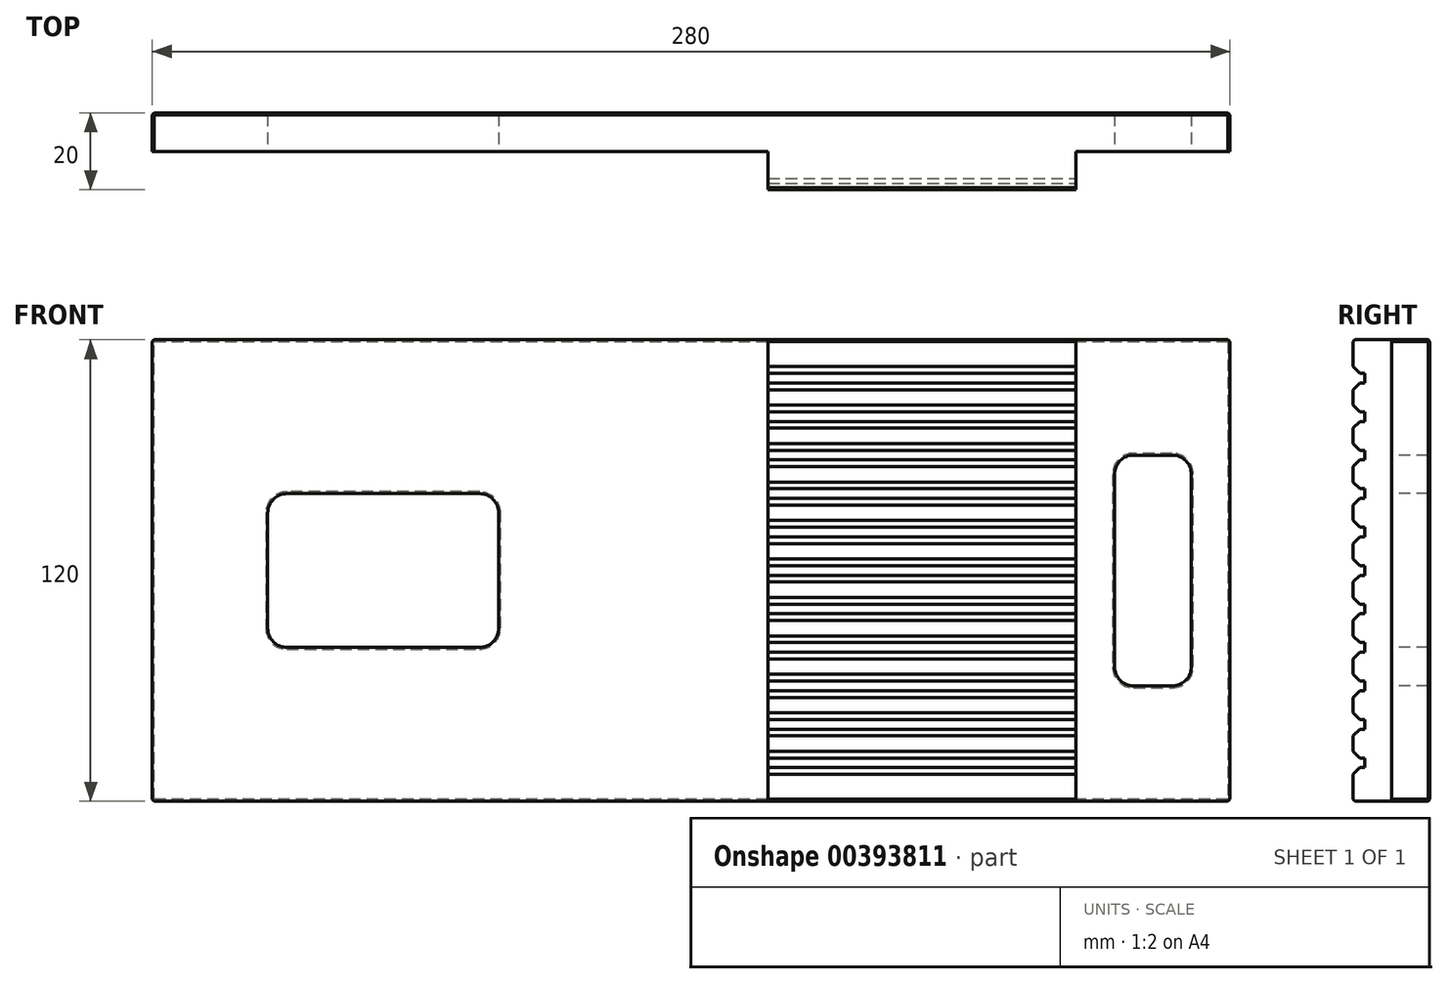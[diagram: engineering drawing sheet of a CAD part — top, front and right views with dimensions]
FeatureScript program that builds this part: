
annotation { "Feature Type Name" : "Feature", "Feature Type Description" : "" }
export const myFeature = defineFeature(function(context is Context, id is Id, definition is map)
    precondition{}
    {
        {
            var Q0;
            Q0=qCreatedBy(makeId("Front.planeOp"),FACE);
            var sketch = newSketch(context, id + "F0", { "sketchPlane" : qUnion([Q0])});
            skLineSegment(sketch, "E0.bottom", {"start": v(140, -60) * mm, "end": v(-140, -60) * mm});
            skLineSegment(sketch, "E0.top", {"start": v(140, 60) * mm, "end": v(-140, 60) * mm});
            skLineSegment(sketch, "E0.left", {"start": v(140, -60) * mm, "end": v(140, 60) * mm});
            skLineSegment(sketch, "E0.right", {"start": v(-140, -60) * mm, "end": v(-140, 60) * mm});
            skPoint(sketch, "E0.middle", {"position": v(0, 0) * mm});
            skSolve(sketch);
        }
        {
            var Q0;
            Q0 = qSketchRegion(id + "F0", true);
            extrude(context, id + "F1", {"entities" : qUnion([Q0]), "depth" : 20 * mm});
        }
        {
            var Q0;
            Q0=makeQuery(id+"F1.opExtrude","CAP_FACE",FACE,{"disambiguationData":[OSD([sQuery(id+"F0.wireOp",EDGE,"E0.bottom"),sQuery(id+"F0.wireOp",EDGE,"E0.top"),sQuery(id+"F0.wireOp",EDGE,"E0.left"),sQuery(id+"F0.wireOp",EDGE,"E0.right")])],"isStart":false});
            var sketch = newSketch(context, id + "F2", { "sketchPlane" : qUnion([Q0])});
            skLineSegment(sketch, "E1.bottom", {"start": v(-140, 60) * mm, "end": v(20, 60) * mm});
            skLineSegment(sketch, "E1.top", {"start": v(-140, -60) * mm, "end": v(20, -60) * mm});
            skLineSegment(sketch, "E1.left", {"start": v(-140, 60) * mm, "end": v(-140, -60) * mm});
            skLineSegment(sketch, "E1.right", {"start": v(20, 60) * mm, "end": v(20, -60) * mm});
            skSolve(sketch);
        }
        {
            var Q0;
            Q0 = qSketchRegion(id + "F2", true);
            extrude(context, id + "F3", {"entities" : qUnion([Q0]), "operationType" : NewBodyOperationType.REMOVE, "oppositeDirection" : true, "depth" : 10 * mm});
        }
        {
            var Q0;
            Q0=makeQuery(id+"F3.boolean.opBoolean","COPY",FACE,{"derivedFrom":makeQuery(id+"F3.opExtrude","CAP_FACE",FACE,{"disambiguationData":[OSD([sQuery(id+"F2.wireOp",EDGE,"E1.bottom"),sQuery(id+"F2.wireOp",EDGE,"E1.top"),sQuery(id+"F2.wireOp",EDGE,"E1.left"),sQuery(id+"F2.wireOp",EDGE,"E1.right")])],"isStart":false})});
            var sketch = newSketch(context, id + "F4", { "sketchPlane" : qUnion([Q0])});
            skLineSegment(sketch, "E2.bottom", {"start": v(-55, -20) * mm, "end": v(-105, -20) * mm});
            skLineSegment(sketch, "E2.top", {"start": v(-55, 20) * mm, "end": v(-105, 20) * mm});
            skLineSegment(sketch, "E2.left", {"start": v(-50, -15) * mm, "end": v(-50, 15) * mm});
            skLineSegment(sketch, "E2.right", {"start": v(-110, -15) * mm, "end": v(-110, 15) * mm});
            skPoint(sketch, "E2.middle", {"position": v(-80, 0) * mm});
            skPoint(sketch, "E3.visualSharp", {"position": v(-50, 20) * mm});
            skArc(sketch, "E3.filletArc", {"start": v(-50, 15) * mm, "mid": v(-51.46, 18.54) * mm, "end": v(-55, 20) * mm});
            skPoint(sketch, "E4.visualSharp", {"position": v(-50, -20) * mm});
            skArc(sketch, "E4.filletArc", {"start": v(-55, -20) * mm, "mid": v(-51.46, -18.54) * mm, "end": v(-50, -15) * mm});
            skPoint(sketch, "E5.visualSharp", {"position": v(-110, -20) * mm});
            skArc(sketch, "E5.filletArc", {"start": v(-110, -15) * mm, "mid": v(-108.54, -18.54) * mm, "end": v(-105, -20) * mm});
            skPoint(sketch, "E6.visualSharp", {"position": v(-110, 20) * mm});
            skArc(sketch, "E6.filletArc", {"start": v(-105, 20) * mm, "mid": v(-108.54, 18.54) * mm, "end": v(-110, 15) * mm});
            skSolve(sketch);
        }
        {
            var Q0;
            Q0 = qSketchRegion(id + "F4", true);
            extrude(context, id + "F5", {"entities" : qUnion([Q0]), "operationType" : NewBodyOperationType.REMOVE, "oppositeDirection" : true, "depth" : 25 * mm});
        }
        {
            var Q0;
            Q0=makeQuery(id+"F1.opExtrude","CAP_FACE",FACE,{"disambiguationData":[OSD([sQuery(id+"F0.wireOp",EDGE,"E0.bottom"),sQuery(id+"F0.wireOp",EDGE,"E0.top"),sQuery(id+"F0.wireOp",EDGE,"E0.left"),sQuery(id+"F0.wireOp",EDGE,"E0.right")])],"isStart":false});
            var sketch = newSketch(context, id + "F6", { "sketchPlane" : qUnion([Q0])});
            skLineSegment(sketch, "E7.bottom", {"start": v(140, -60) * mm, "end": v(100, -60) * mm});
            skLineSegment(sketch, "E7.top", {"start": v(140, 60) * mm, "end": v(100, 60) * mm});
            skLineSegment(sketch, "E7.left", {"start": v(140, -60) * mm, "end": v(140, 60) * mm});
            skLineSegment(sketch, "E7.right", {"start": v(100, -60) * mm, "end": v(100, 60) * mm});
            skPoint(sketch, "E7.middle", {"position": v(120, 0) * mm});
            skSolve(sketch);
        }
        {
            var Q0;
            Q0 = qSketchRegion(id + "F6", true);
            extrude(context, id + "F7", {"entities" : qUnion([Q0]), "operationType" : NewBodyOperationType.REMOVE, "oppositeDirection" : true, "depth" : 10 * mm});
        }
        {
            var Q0;
            Q0=makeQuery(id+"F7.boolean.opBoolean","COPY",FACE,{"derivedFrom":makeQuery(id+"F7.opExtrude","CAP_FACE",FACE,{"disambiguationData":[OSD([sQuery(id+"F6.wireOp",EDGE,"E7.bottom"),sQuery(id+"F6.wireOp",EDGE,"E7.top"),sQuery(id+"F6.wireOp",EDGE,"E7.left"),sQuery(id+"F6.wireOp",EDGE,"E7.right")])],"isStart":false})});
            var sketch = newSketch(context, id + "F8", { "sketchPlane" : qUnion([Q0])});
            skLineSegment(sketch, "E8.bottom", {"start": v(115, -30) * mm, "end": v(125, -30) * mm});
            skLineSegment(sketch, "E8.top", {"start": v(115, 30) * mm, "end": v(125, 30) * mm});
            skLineSegment(sketch, "E8.left", {"start": v(110, -25) * mm, "end": v(110, 25) * mm});
            skLineSegment(sketch, "E8.right", {"start": v(130, -25) * mm, "end": v(130, 25) * mm});
            skPoint(sketch, "E8.middle", {"position": v(120, 0) * mm});
            skPoint(sketch, "E9", {"position": v(140, 0) * mm});
            skPoint(sketch, "E10.visualSharp", {"position": v(110, 30) * mm});
            skArc(sketch, "E10.filletArc", {"start": v(115, 30) * mm, "mid": v(111.46, 28.54) * mm, "end": v(110, 25) * mm});
            skPoint(sketch, "E11.visualSharp", {"position": v(130, 30) * mm});
            skArc(sketch, "E11.filletArc", {"start": v(130, 25) * mm, "mid": v(128.54, 28.54) * mm, "end": v(125, 30) * mm});
            skPoint(sketch, "E12.visualSharp", {"position": v(130, -30) * mm});
            skArc(sketch, "E12.filletArc", {"start": v(125, -30) * mm, "mid": v(128.54, -28.54) * mm, "end": v(130, -25) * mm});
            skPoint(sketch, "E13.visualSharp", {"position": v(110, -30) * mm});
            skArc(sketch, "E13.filletArc", {"start": v(110, -25) * mm, "mid": v(111.46, -28.54) * mm, "end": v(115, -30) * mm});
            skSolve(sketch);
        }
        {
            var Q0;
            Q0 = qSketchRegion(id + "F8", true);
            extrude(context, id + "F9", {"entities" : qUnion([Q0]), "operationType" : NewBodyOperationType.REMOVE, "endBound" : BoundingType.THROUGH_ALL, "oppositeDirection" : true, "depth" : 25 * mm});
        }
        {
            var Q0;
            Q0=makeQuery(id+"F7.boolean.opBoolean","COPY",FACE,{"derivedFrom":makeQuery(id+"F7.opExtrude","SWEPT_FACE",FACE,{"disambiguationData":[OSD([sQuery(id+"F6.wireOp",EDGE,"E7.right")])]})});
            var sketch = newSketch(context, id + "F10", { "sketchPlane" : qUnion([Q0])});
            skLineSegment(sketch, "E14", {"start": v(-20, -50) * mm, "end": v(-17, -50) * mm, "construction": true});
            skLineSegment(sketch, "E15", {"start": v(-17, -51.25) * mm, "end": v(-17, -48.75) * mm});
            skLineSegment(sketch, "E16", {"start": v(-17, -51.25) * mm, "end": v(-18.25, -51.25) * mm});
            skLineSegment(sketch, "E17", {"start": v(-17, -48.75) * mm, "end": v(-18.25, -48.75) * mm});
            skLineSegment(sketch, "E18", {"start": v(-20, -53) * mm, "end": v(-18.25, -51.25) * mm});
            skLineSegment(sketch, "E19", {"start": v(-18.25, -48.75) * mm, "end": v(-20, -47) * mm});
            skLineSegment(sketch, "E20", {"start": v(-20, -53) * mm, "end": v(-20, -47) * mm});
            skLineSegment(sketch, "E21.0.1.0", {"start": v(-20, -43) * mm, "end": v(-20, -37) * mm});
            skLineSegment(sketch, "E21.0.1.1", {"start": v(-20, -43) * mm, "end": v(-18.25, -41.25) * mm});
            skLineSegment(sketch, "E21.0.1.2", {"start": v(-17, -41.25) * mm, "end": v(-18.25, -41.25) * mm});
            skLineSegment(sketch, "E21.0.1.3", {"start": v(-17, -41.25) * mm, "end": v(-17, -38.75) * mm});
            skLineSegment(sketch, "E21.0.1.4", {"start": v(-17, -38.75) * mm, "end": v(-18.25, -38.75) * mm});
            skLineSegment(sketch, "E21.0.1.5", {"start": v(-18.25, -38.75) * mm, "end": v(-20, -37) * mm});
            skLineSegment(sketch, "E21.0.2.0", {"start": v(-20, -33) * mm, "end": v(-20, -27) * mm});
            skLineSegment(sketch, "E21.0.2.1", {"start": v(-20, -33) * mm, "end": v(-18.25, -31.25) * mm});
            skLineSegment(sketch, "E21.0.2.2", {"start": v(-17, -31.25) * mm, "end": v(-18.25, -31.25) * mm});
            skLineSegment(sketch, "E21.0.2.3", {"start": v(-17, -31.25) * mm, "end": v(-17, -28.75) * mm});
            skLineSegment(sketch, "E21.0.2.4", {"start": v(-17, -28.75) * mm, "end": v(-18.25, -28.75) * mm});
            skLineSegment(sketch, "E21.0.2.5", {"start": v(-18.25, -28.75) * mm, "end": v(-20, -27) * mm});
            skLineSegment(sketch, "E21.0.3.0", {"start": v(-20, -23) * mm, "end": v(-20, -17) * mm});
            skLineSegment(sketch, "E21.0.3.1", {"start": v(-20, -23) * mm, "end": v(-18.25, -21.25) * mm});
            skLineSegment(sketch, "E21.0.3.2", {"start": v(-17, -21.25) * mm, "end": v(-18.25, -21.25) * mm});
            skLineSegment(sketch, "E21.0.3.3", {"start": v(-17, -21.25) * mm, "end": v(-17, -18.75) * mm});
            skLineSegment(sketch, "E21.0.3.4", {"start": v(-17, -18.75) * mm, "end": v(-18.25, -18.75) * mm});
            skLineSegment(sketch, "E21.0.3.5", {"start": v(-18.25, -18.75) * mm, "end": v(-20, -17) * mm});
            skLineSegment(sketch, "E21.0.4.0", {"start": v(-20, -13) * mm, "end": v(-20, -7) * mm});
            skLineSegment(sketch, "E21.0.4.1", {"start": v(-20, -13) * mm, "end": v(-18.25, -11.25) * mm});
            skLineSegment(sketch, "E21.0.4.2", {"start": v(-17, -11.25) * mm, "end": v(-18.25, -11.25) * mm});
            skLineSegment(sketch, "E21.0.4.3", {"start": v(-17, -11.25) * mm, "end": v(-17, -8.75) * mm});
            skLineSegment(sketch, "E21.0.4.4", {"start": v(-17, -8.75) * mm, "end": v(-18.25, -8.75) * mm});
            skLineSegment(sketch, "E21.0.4.5", {"start": v(-18.25, -8.75) * mm, "end": v(-20, -7) * mm});
            skLineSegment(sketch, "E21.0.5.0", {"start": v(-20, -3) * mm, "end": v(-20, 3) * mm});
            skLineSegment(sketch, "E21.0.5.1", {"start": v(-20, -3) * mm, "end": v(-18.25, -1.25) * mm});
            skLineSegment(sketch, "E21.0.5.2", {"start": v(-17, -1.25) * mm, "end": v(-18.25, -1.25) * mm});
            skLineSegment(sketch, "E21.0.5.3", {"start": v(-17, -1.25) * mm, "end": v(-17, 1.25) * mm});
            skLineSegment(sketch, "E21.0.5.4", {"start": v(-17, 1.25) * mm, "end": v(-18.25, 1.25) * mm});
            skLineSegment(sketch, "E21.0.5.5", {"start": v(-18.25, 1.25) * mm, "end": v(-20, 3) * mm});
            skLineSegment(sketch, "E21.0.6.0", {"start": v(-20, 7) * mm, "end": v(-20, 13) * mm});
            skLineSegment(sketch, "E21.0.6.1", {"start": v(-20, 7) * mm, "end": v(-18.25, 8.75) * mm});
            skLineSegment(sketch, "E21.0.6.2", {"start": v(-17, 8.75) * mm, "end": v(-18.25, 8.75) * mm});
            skLineSegment(sketch, "E21.0.6.3", {"start": v(-17, 8.75) * mm, "end": v(-17, 11.25) * mm});
            skLineSegment(sketch, "E21.0.6.4", {"start": v(-17, 11.25) * mm, "end": v(-18.25, 11.25) * mm});
            skLineSegment(sketch, "E21.0.6.5", {"start": v(-18.25, 11.25) * mm, "end": v(-20, 13) * mm});
            skLineSegment(sketch, "E21.0.7.0", {"start": v(-20, 17) * mm, "end": v(-20, 23) * mm});
            skLineSegment(sketch, "E21.0.7.1", {"start": v(-20, 17) * mm, "end": v(-18.25, 18.75) * mm});
            skLineSegment(sketch, "E21.0.7.2", {"start": v(-17, 18.75) * mm, "end": v(-18.25, 18.75) * mm});
            skLineSegment(sketch, "E21.0.7.3", {"start": v(-17, 18.75) * mm, "end": v(-17, 21.25) * mm});
            skLineSegment(sketch, "E21.0.7.4", {"start": v(-17, 21.25) * mm, "end": v(-18.25, 21.25) * mm});
            skLineSegment(sketch, "E21.0.7.5", {"start": v(-18.25, 21.25) * mm, "end": v(-20, 23) * mm});
            skLineSegment(sketch, "E21.0.8.0", {"start": v(-20, 27) * mm, "end": v(-20, 33) * mm});
            skLineSegment(sketch, "E21.0.8.1", {"start": v(-20, 27) * mm, "end": v(-18.25, 28.75) * mm});
            skLineSegment(sketch, "E21.0.8.2", {"start": v(-17, 28.75) * mm, "end": v(-18.25, 28.75) * mm});
            skLineSegment(sketch, "E21.0.8.3", {"start": v(-17, 28.75) * mm, "end": v(-17, 31.25) * mm});
            skLineSegment(sketch, "E21.0.8.4", {"start": v(-17, 31.25) * mm, "end": v(-18.25, 31.25) * mm});
            skLineSegment(sketch, "E21.0.8.5", {"start": v(-18.25, 31.25) * mm, "end": v(-20, 33) * mm});
            skLineSegment(sketch, "E21.0.9.0", {"start": v(-20, 37) * mm, "end": v(-20, 43) * mm});
            skLineSegment(sketch, "E21.0.9.1", {"start": v(-20, 37) * mm, "end": v(-18.25, 38.75) * mm});
            skLineSegment(sketch, "E21.0.9.2", {"start": v(-17, 38.75) * mm, "end": v(-18.25, 38.75) * mm});
            skLineSegment(sketch, "E21.0.9.3", {"start": v(-17, 38.75) * mm, "end": v(-17, 41.25) * mm});
            skLineSegment(sketch, "E21.0.9.4", {"start": v(-17, 41.25) * mm, "end": v(-18.25, 41.25) * mm});
            skLineSegment(sketch, "E21.0.9.5", {"start": v(-18.25, 41.25) * mm, "end": v(-20, 43) * mm});
            skLineSegment(sketch, "E21.0.10.0", {"start": v(-20, 47) * mm, "end": v(-20, 53) * mm});
            skLineSegment(sketch, "E21.0.10.1", {"start": v(-20, 47) * mm, "end": v(-18.25, 48.75) * mm});
            skLineSegment(sketch, "E21.0.10.2", {"start": v(-17, 48.75) * mm, "end": v(-18.25, 48.75) * mm});
            skLineSegment(sketch, "E21.0.10.3", {"start": v(-17, 48.75) * mm, "end": v(-17, 51.25) * mm});
            skLineSegment(sketch, "E21.0.10.4", {"start": v(-17, 51.25) * mm, "end": v(-18.25, 51.25) * mm});
            skLineSegment(sketch, "E21.0.10.5", {"start": v(-18.25, 51.25) * mm, "end": v(-20, 53) * mm});
            skLineSegment(sketch, "E21.direction1", {"start": v(-20, -53) * mm, "end": v(5, -53) * mm, "construction": true});
            skLineSegment(sketch, "E21.direction2", {"start": v(-20, -53) * mm, "end": v(-20, -43) * mm, "construction": true});
            skSolve(sketch);
        }
        {
            var Q0;
            Q0 = qSketchRegion(id + "F10", true);
            extrude(context, id + "F11", {"entities" : qUnion([Q0]), "operationType" : NewBodyOperationType.REMOVE, "endBound" : BoundingType.THROUGH_ALL, "oppositeDirection" : true, "depth" : 25 * mm});
        }
        {
            var Q0;
            Q0=makeQuery(id+"F1.opExtrude","CAP_EDGE",EDGE,{"disambiguationData":[OSD([sQuery(id+"F0.wireOp",EDGE,"E0.bottom")])],"isStart":false});
            var Q1;
            {var subQ0=sQuery(id+"F0.wireOp",EDGE,"E0.bottom");var subQ1=sQuery(id+"F6.wireOp",EDGE,"E7.right");Q1=makeQuery(id+"F11.boolean.opBoolean","SPLIT",EDGE,{"disambiguationData":[TD([makeQuery(id+"F1.opExtrude","SWEPT_FACE",FACE,{"disambiguationData":[OSD([subQ0])]})])],"derivedFrom":makeQuery(id+"F7.boolean.opBoolean","COPY",EDGE,{"derivedFrom":makeQuery(id+"F7.opExtrude","CAP_EDGE",EDGE,{"disambiguationData":[OSD([subQ1])],"isStart":true})})});}
            var Q2;
            {var subQ0=sQuery(id+"F6.wireOp",EDGE,"E7.right");Q2=makeQuery(id+"F11.boolean.opBoolean","SPLIT",EDGE,{"disambiguationData":[TD([makeQuery(id+"F11.opExtrude","SWEPT_FACE",FACE,{"disambiguationData":[OSD([sQuery(id+"F10.wireOp",EDGE,"E19")])]})])],"derivedFrom":makeQuery(id+"F7.boolean.opBoolean","COPY",EDGE,{"derivedFrom":makeQuery(id+"F7.opExtrude","CAP_EDGE",EDGE,{"disambiguationData":[OSD([subQ0])],"isStart":true})})});}
            var Q3;
            {var subQ0=sQuery(id+"F6.wireOp",EDGE,"E7.right");Q3=makeQuery(id+"F11.boolean.opBoolean","SPLIT",EDGE,{"disambiguationData":[TD([makeQuery(id+"F11.opExtrude","SWEPT_FACE",FACE,{"disambiguationData":[OSD([sQuery(id+"F10.wireOp",EDGE,"E21.0.2.5")])]})])],"derivedFrom":makeQuery(id+"F7.boolean.opBoolean","COPY",EDGE,{"derivedFrom":makeQuery(id+"F7.opExtrude","CAP_EDGE",EDGE,{"disambiguationData":[OSD([subQ0])],"isStart":true})})});}
            var Q4;
            {var subQ0=sQuery(id+"F6.wireOp",EDGE,"E7.right");Q4=makeQuery(id+"F11.boolean.opBoolean","SPLIT",EDGE,{"disambiguationData":[TD([makeQuery(id+"F11.opExtrude","SWEPT_FACE",FACE,{"disambiguationData":[OSD([sQuery(id+"F10.wireOp",EDGE,"E21.0.3.5")])]})])],"derivedFrom":makeQuery(id+"F7.boolean.opBoolean","COPY",EDGE,{"derivedFrom":makeQuery(id+"F7.opExtrude","CAP_EDGE",EDGE,{"disambiguationData":[OSD([subQ0])],"isStart":true})})});}
            var Q5;
            {var subQ0=sQuery(id+"F6.wireOp",EDGE,"E7.right");Q5=makeQuery(id+"F11.boolean.opBoolean","SPLIT",EDGE,{"disambiguationData":[TD([makeQuery(id+"F11.opExtrude","SWEPT_FACE",FACE,{"disambiguationData":[OSD([sQuery(id+"F10.wireOp",EDGE,"E21.0.1.5")])]})])],"derivedFrom":makeQuery(id+"F7.boolean.opBoolean","COPY",EDGE,{"derivedFrom":makeQuery(id+"F7.opExtrude","CAP_EDGE",EDGE,{"disambiguationData":[OSD([subQ0])],"isStart":true})})});}
            var Q6;
            {var subQ0=sQuery(id+"F6.wireOp",EDGE,"E7.right");Q6=makeQuery(id+"F11.boolean.opBoolean","SPLIT",EDGE,{"disambiguationData":[TD([makeQuery(id+"F11.opExtrude","SWEPT_FACE",FACE,{"disambiguationData":[OSD([sQuery(id+"F10.wireOp",EDGE,"E21.0.4.5")])]})])],"derivedFrom":makeQuery(id+"F7.boolean.opBoolean","COPY",EDGE,{"derivedFrom":makeQuery(id+"F7.opExtrude","CAP_EDGE",EDGE,{"disambiguationData":[OSD([subQ0])],"isStart":true})})});}
            var Q7;
            {var subQ0=sQuery(id+"F6.wireOp",EDGE,"E7.right");Q7=makeQuery(id+"F11.boolean.opBoolean","SPLIT",EDGE,{"disambiguationData":[TD([makeQuery(id+"F11.opExtrude","SWEPT_FACE",FACE,{"disambiguationData":[OSD([sQuery(id+"F10.wireOp",EDGE,"E21.0.5.5")])]})])],"derivedFrom":makeQuery(id+"F7.boolean.opBoolean","COPY",EDGE,{"derivedFrom":makeQuery(id+"F7.opExtrude","CAP_EDGE",EDGE,{"disambiguationData":[OSD([subQ0])],"isStart":true})})});}
            var Q8;
            {var subQ0=sQuery(id+"F6.wireOp",EDGE,"E7.right");Q8=makeQuery(id+"F11.boolean.opBoolean","SPLIT",EDGE,{"disambiguationData":[TD([makeQuery(id+"F11.opExtrude","SWEPT_FACE",FACE,{"disambiguationData":[OSD([sQuery(id+"F10.wireOp",EDGE,"E21.0.6.5")])]})])],"derivedFrom":makeQuery(id+"F7.boolean.opBoolean","COPY",EDGE,{"derivedFrom":makeQuery(id+"F7.opExtrude","CAP_EDGE",EDGE,{"disambiguationData":[OSD([subQ0])],"isStart":true})})});}
            var Q9;
            {var subQ0=sQuery(id+"F6.wireOp",EDGE,"E7.right");Q9=makeQuery(id+"F11.boolean.opBoolean","SPLIT",EDGE,{"disambiguationData":[TD([makeQuery(id+"F11.opExtrude","SWEPT_FACE",FACE,{"disambiguationData":[OSD([sQuery(id+"F10.wireOp",EDGE,"E21.0.7.5")])]})])],"derivedFrom":makeQuery(id+"F7.boolean.opBoolean","COPY",EDGE,{"derivedFrom":makeQuery(id+"F7.opExtrude","CAP_EDGE",EDGE,{"disambiguationData":[OSD([subQ0])],"isStart":true})})});}
            var Q10;
            {var subQ0=sQuery(id+"F6.wireOp",EDGE,"E7.right");Q10=makeQuery(id+"F11.boolean.opBoolean","SPLIT",EDGE,{"disambiguationData":[TD([makeQuery(id+"F11.opExtrude","SWEPT_FACE",FACE,{"disambiguationData":[OSD([sQuery(id+"F10.wireOp",EDGE,"E21.0.8.5")])]})])],"derivedFrom":makeQuery(id+"F7.boolean.opBoolean","COPY",EDGE,{"derivedFrom":makeQuery(id+"F7.opExtrude","CAP_EDGE",EDGE,{"disambiguationData":[OSD([subQ0])],"isStart":true})})});}
            var Q11;
            {var subQ0=sQuery(id+"F6.wireOp",EDGE,"E7.right");Q11=makeQuery(id+"F11.boolean.opBoolean","SPLIT",EDGE,{"disambiguationData":[TD([makeQuery(id+"F11.opExtrude","SWEPT_FACE",FACE,{"disambiguationData":[OSD([sQuery(id+"F10.wireOp",EDGE,"E21.0.9.5")])]})])],"derivedFrom":makeQuery(id+"F7.boolean.opBoolean","COPY",EDGE,{"derivedFrom":makeQuery(id+"F7.opExtrude","CAP_EDGE",EDGE,{"disambiguationData":[OSD([subQ0])],"isStart":true})})});}
            var Q12;
            {var subQ0=sQuery(id+"F0.wireOp",EDGE,"E0.top");var subQ1=sQuery(id+"F6.wireOp",EDGE,"E7.right");Q12=makeQuery(id+"F11.boolean.opBoolean","SPLIT",EDGE,{"disambiguationData":[TD([makeQuery(id+"F1.opExtrude","SWEPT_FACE",FACE,{"disambiguationData":[OSD([subQ0])]})])],"derivedFrom":makeQuery(id+"F7.boolean.opBoolean","COPY",EDGE,{"derivedFrom":makeQuery(id+"F7.opExtrude","CAP_EDGE",EDGE,{"disambiguationData":[OSD([subQ1])],"isStart":true})})});}
            var Q13;
            Q13=makeQuery(id+"F1.opExtrude","CAP_EDGE",EDGE,{"disambiguationData":[OSD([sQuery(id+"F0.wireOp",EDGE,"E0.top")])],"isStart":false});
            var Q14;
            {var subQ0=sQuery(id+"F0.wireOp",EDGE,"E0.bottom");var subQ1=sQuery(id+"F2.wireOp",EDGE,"E1.right");Q14=makeQuery(id+"F11.boolean.opBoolean","SPLIT",EDGE,{"disambiguationData":[TD([makeQuery(id+"F1.opExtrude","SWEPT_FACE",FACE,{"disambiguationData":[OSD([subQ0])]})])],"derivedFrom":makeQuery(id+"F3.boolean.opBoolean","COPY",EDGE,{"derivedFrom":makeQuery(id+"F3.opExtrude","CAP_EDGE",EDGE,{"disambiguationData":[OSD([subQ1])],"isStart":true})})});}
            var Q15;
            {var subQ0=sQuery(id+"F2.wireOp",EDGE,"E1.right");Q15=makeQuery(id+"F11.boolean.opBoolean","SPLIT",EDGE,{"disambiguationData":[TD([makeQuery(id+"F11.opExtrude","SWEPT_FACE",FACE,{"disambiguationData":[OSD([sQuery(id+"F10.wireOp",EDGE,"E19")])]})])],"derivedFrom":makeQuery(id+"F3.boolean.opBoolean","COPY",EDGE,{"derivedFrom":makeQuery(id+"F3.opExtrude","CAP_EDGE",EDGE,{"disambiguationData":[OSD([subQ0])],"isStart":true})})});}
            var Q16;
            {var subQ0=sQuery(id+"F2.wireOp",EDGE,"E1.right");Q16=makeQuery(id+"F11.boolean.opBoolean","SPLIT",EDGE,{"disambiguationData":[TD([makeQuery(id+"F11.opExtrude","SWEPT_FACE",FACE,{"disambiguationData":[OSD([sQuery(id+"F10.wireOp",EDGE,"E21.0.1.5")])]})])],"derivedFrom":makeQuery(id+"F3.boolean.opBoolean","COPY",EDGE,{"derivedFrom":makeQuery(id+"F3.opExtrude","CAP_EDGE",EDGE,{"disambiguationData":[OSD([subQ0])],"isStart":true})})});}
            var Q17;
            {var subQ0=sQuery(id+"F2.wireOp",EDGE,"E1.right");Q17=makeQuery(id+"F11.boolean.opBoolean","SPLIT",EDGE,{"disambiguationData":[TD([makeQuery(id+"F11.opExtrude","SWEPT_FACE",FACE,{"disambiguationData":[OSD([sQuery(id+"F10.wireOp",EDGE,"E21.0.2.5")])]})])],"derivedFrom":makeQuery(id+"F3.boolean.opBoolean","COPY",EDGE,{"derivedFrom":makeQuery(id+"F3.opExtrude","CAP_EDGE",EDGE,{"disambiguationData":[OSD([subQ0])],"isStart":true})})});}
            var Q18;
            {var subQ0=sQuery(id+"F2.wireOp",EDGE,"E1.right");Q18=makeQuery(id+"F11.boolean.opBoolean","SPLIT",EDGE,{"disambiguationData":[TD([makeQuery(id+"F11.opExtrude","SWEPT_FACE",FACE,{"disambiguationData":[OSD([sQuery(id+"F10.wireOp",EDGE,"E21.0.3.5")])]})])],"derivedFrom":makeQuery(id+"F3.boolean.opBoolean","COPY",EDGE,{"derivedFrom":makeQuery(id+"F3.opExtrude","CAP_EDGE",EDGE,{"disambiguationData":[OSD([subQ0])],"isStart":true})})});}
            var Q19;
            {var subQ0=sQuery(id+"F2.wireOp",EDGE,"E1.right");Q19=makeQuery(id+"F11.boolean.opBoolean","SPLIT",EDGE,{"disambiguationData":[TD([makeQuery(id+"F11.opExtrude","SWEPT_FACE",FACE,{"disambiguationData":[OSD([sQuery(id+"F10.wireOp",EDGE,"E21.0.4.5")])]})])],"derivedFrom":makeQuery(id+"F3.boolean.opBoolean","COPY",EDGE,{"derivedFrom":makeQuery(id+"F3.opExtrude","CAP_EDGE",EDGE,{"disambiguationData":[OSD([subQ0])],"isStart":true})})});}
            var Q20;
            {var subQ0=sQuery(id+"F2.wireOp",EDGE,"E1.right");Q20=makeQuery(id+"F11.boolean.opBoolean","SPLIT",EDGE,{"disambiguationData":[TD([makeQuery(id+"F11.opExtrude","SWEPT_FACE",FACE,{"disambiguationData":[OSD([sQuery(id+"F10.wireOp",EDGE,"E21.0.5.5")])]})])],"derivedFrom":makeQuery(id+"F3.boolean.opBoolean","COPY",EDGE,{"derivedFrom":makeQuery(id+"F3.opExtrude","CAP_EDGE",EDGE,{"disambiguationData":[OSD([subQ0])],"isStart":true})})});}
            var Q21;
            {var subQ0=sQuery(id+"F2.wireOp",EDGE,"E1.right");Q21=makeQuery(id+"F11.boolean.opBoolean","SPLIT",EDGE,{"disambiguationData":[TD([makeQuery(id+"F11.opExtrude","SWEPT_FACE",FACE,{"disambiguationData":[OSD([sQuery(id+"F10.wireOp",EDGE,"E21.0.6.5")])]})])],"derivedFrom":makeQuery(id+"F3.boolean.opBoolean","COPY",EDGE,{"derivedFrom":makeQuery(id+"F3.opExtrude","CAP_EDGE",EDGE,{"disambiguationData":[OSD([subQ0])],"isStart":true})})});}
            var Q22;
            {var subQ0=sQuery(id+"F2.wireOp",EDGE,"E1.right");Q22=makeQuery(id+"F11.boolean.opBoolean","SPLIT",EDGE,{"disambiguationData":[TD([makeQuery(id+"F11.opExtrude","SWEPT_FACE",FACE,{"disambiguationData":[OSD([sQuery(id+"F10.wireOp",EDGE,"E21.0.7.5")])]})])],"derivedFrom":makeQuery(id+"F3.boolean.opBoolean","COPY",EDGE,{"derivedFrom":makeQuery(id+"F3.opExtrude","CAP_EDGE",EDGE,{"disambiguationData":[OSD([subQ0])],"isStart":true})})});}
            var Q23;
            {var subQ0=sQuery(id+"F0.wireOp",EDGE,"E0.top");var subQ1=sQuery(id+"F2.wireOp",EDGE,"E1.right");Q23=makeQuery(id+"F11.boolean.opBoolean","SPLIT",EDGE,{"disambiguationData":[TD([makeQuery(id+"F1.opExtrude","SWEPT_FACE",FACE,{"disambiguationData":[OSD([subQ0])]})])],"derivedFrom":makeQuery(id+"F3.boolean.opBoolean","COPY",EDGE,{"derivedFrom":makeQuery(id+"F3.opExtrude","CAP_EDGE",EDGE,{"disambiguationData":[OSD([subQ1])],"isStart":true})})});}
            var Q24;
            {var subQ0=sQuery(id+"F2.wireOp",EDGE,"E1.right");Q24=makeQuery(id+"F11.boolean.opBoolean","SPLIT",EDGE,{"disambiguationData":[TD([makeQuery(id+"F11.opExtrude","SWEPT_FACE",FACE,{"disambiguationData":[OSD([sQuery(id+"F10.wireOp",EDGE,"E21.0.9.5")])]})])],"derivedFrom":makeQuery(id+"F3.boolean.opBoolean","COPY",EDGE,{"derivedFrom":makeQuery(id+"F3.opExtrude","CAP_EDGE",EDGE,{"disambiguationData":[OSD([subQ0])],"isStart":true})})});}
            var Q25;
            {var subQ0=sQuery(id+"F2.wireOp",EDGE,"E1.right");Q25=makeQuery(id+"F11.boolean.opBoolean","SPLIT",EDGE,{"disambiguationData":[TD([makeQuery(id+"F11.opExtrude","SWEPT_FACE",FACE,{"disambiguationData":[OSD([sQuery(id+"F10.wireOp",EDGE,"E21.0.8.5")])]})])],"derivedFrom":makeQuery(id+"F3.boolean.opBoolean","COPY",EDGE,{"derivedFrom":makeQuery(id+"F3.opExtrude","CAP_EDGE",EDGE,{"disambiguationData":[OSD([subQ0])],"isStart":true})})});}
            chamfer(context, id + "F12", {"entities" : qUnion([Q0, Q1, Q2, Q3, Q4, Q5, Q6, Q7, Q8, Q9, Q10, Q11, Q12, Q13, Q14, Q15, Q16, Q17, Q18, Q19, Q20, Q21, Q22, Q23, Q24, Q25]), "width" : 0.5 * mm, "tangentPropagation" : true});
        }
        {
            var Q0;
            Q0=makeQuery(id+"F9.boolean.opBoolean","COPY",EDGE,{"derivedFrom":makeQuery(id+"F9.opExtrude","CAP_EDGE",EDGE,{"disambiguationData":[OSD([sQuery(id+"F8.wireOp",EDGE,"E8.left")])],"isStart":true})});
            var Q1;
            Q1=makeQuery(id+"F5.boolean.opBoolean","COPY",EDGE,{"derivedFrom":makeQuery(id+"F5.opExtrude","CAP_EDGE",EDGE,{"disambiguationData":[OSD([sQuery(id+"F4.wireOp",EDGE,"E2.bottom")])],"isStart":true})});
            var Q2;
            Q2=makeQuery(id+"F5.boolean.opBoolean","INTERSECT",EDGE,{"derivedFrom":[makeQuery(id+"F1.opExtrude","CAP_FACE",FACE,{"disambiguationData":[OSD([sQuery(id+"F0.wireOp",EDGE,"E0.bottom"),sQuery(id+"F0.wireOp",EDGE,"E0.top"),sQuery(id+"F0.wireOp",EDGE,"E0.left"),sQuery(id+"F0.wireOp",EDGE,"E0.right")])],"isStart":true}),makeQuery(id+"F5.opExtrude","SWEPT_FACE",FACE,{"disambiguationData":[OSD([sQuery(id+"F4.wireOp",EDGE,"E2.bottom")])]})]});
            var Q3;
            Q3=makeQuery(id+"F9.boolean.opBoolean","INTERSECT",EDGE,{"derivedFrom":[makeQuery(id+"F1.opExtrude","CAP_FACE",FACE,{"disambiguationData":[OSD([sQuery(id+"F0.wireOp",EDGE,"E0.bottom"),sQuery(id+"F0.wireOp",EDGE,"E0.top"),sQuery(id+"F0.wireOp",EDGE,"E0.left"),sQuery(id+"F0.wireOp",EDGE,"E0.right")])],"isStart":true}),makeQuery(id+"F9.opExtrude","SWEPT_FACE",FACE,{"disambiguationData":[OSD([sQuery(id+"F8.wireOp",EDGE,"E8.left")])]})]});
            chamfer(context, id + "F13", {"entities" : qUnion([Q0, Q1, Q2, Q3]), "width" : 0.5 * mm, "tangentPropagation" : true});
        }
        {
            var Q0;
            Q0=makeQuery(id+"F1.opExtrude","SWEPT_EDGE",EDGE,{"disambiguationData":[OSD([sQuery(id+"F0.wireOp",EDGE,"E0.top"),sQuery(id+"F0.wireOp",EDGE,"E0.right")])]});
            var Q1;
            Q1=makeQuery(id+"F3.boolean.opBoolean","COPY",EDGE,{"derivedFrom":makeQuery(id+"F3.opExtrude","CAP_EDGE",EDGE,{"disambiguationData":[OSD([sQuery(id+"F2.wireOp",EDGE,"E1.left")])],"isStart":false})});
            var Q2;
            Q2=makeQuery(id+"F1.opExtrude","CAP_EDGE",EDGE,{"disambiguationData":[OSD([sQuery(id+"F0.wireOp",EDGE,"E0.right")])],"isStart":true});
            var Q3;
            Q3=makeQuery(id+"F1.opExtrude","SWEPT_EDGE",EDGE,{"disambiguationData":[OSD([sQuery(id+"F0.wireOp",EDGE,"E0.bottom"),sQuery(id+"F0.wireOp",EDGE,"E0.right")])]});
            var Q4;
            Q4=makeQuery(id+"F3.boolean.opBoolean","COPY",EDGE,{"derivedFrom":makeQuery(id+"F3.opExtrude","CAP_EDGE",EDGE,{"disambiguationData":[OSD([sQuery(id+"F2.wireOp",EDGE,"E1.bottom")])],"isStart":false})});
            var Q5;
            Q5=makeQuery(id+"F1.opExtrude","CAP_EDGE",EDGE,{"disambiguationData":[OSD([sQuery(id+"F0.wireOp",EDGE,"E0.top")])],"isStart":true});
            var Q6;
            Q6=makeQuery(id+"F3.boolean.opBoolean","COPY",EDGE,{"derivedFrom":makeQuery(id+"F3.opExtrude","SWEPT_EDGE",EDGE,{"disambiguationData":[OSD([sQuery(id+"F0.wireOp",EDGE,"E0.top"),sQuery(id+"F2.wireOp",EDGE,"E1.bottom"),sQuery(id+"F2.wireOp",EDGE,"E1.right")])]})});
            var Q7;
            Q7=makeQuery(id+"F3.boolean.opBoolean","COPY",EDGE,{"derivedFrom":makeQuery(id+"F3.opExtrude","SWEPT_EDGE",EDGE,{"disambiguationData":[OSD([sQuery(id+"F0.wireOp",EDGE,"E0.bottom"),sQuery(id+"F2.wireOp",EDGE,"E1.top"),sQuery(id+"F2.wireOp",EDGE,"E1.right")])]})});
            var Q8;
            Q8=makeQuery(id+"F3.boolean.opBoolean","COPY",EDGE,{"derivedFrom":makeQuery(id+"F3.opExtrude","CAP_EDGE",EDGE,{"disambiguationData":[OSD([sQuery(id+"F2.wireOp",EDGE,"E1.top")])],"isStart":false})});
            var Q9;
            Q9=makeQuery(id+"F1.opExtrude","CAP_EDGE",EDGE,{"disambiguationData":[OSD([sQuery(id+"F0.wireOp",EDGE,"E0.bottom")])],"isStart":true});
            var Q10;
            Q10=makeQuery(id+"F1.opExtrude","SWEPT_EDGE",EDGE,{"disambiguationData":[OSD([sQuery(id+"F0.wireOp",EDGE,"E0.top"),sQuery(id+"F0.wireOp",EDGE,"E0.left")])]});
            var Q11;
            Q11=makeQuery(id+"F1.opExtrude","CAP_EDGE",EDGE,{"disambiguationData":[OSD([sQuery(id+"F0.wireOp",EDGE,"E0.left")])],"isStart":true});
            var Q12;
            Q12=makeQuery(id+"F7.boolean.opBoolean","COPY",EDGE,{"derivedFrom":makeQuery(id+"F7.opExtrude","CAP_EDGE",EDGE,{"disambiguationData":[OSD([sQuery(id+"F6.wireOp",EDGE,"E7.left")])],"isStart":false})});
            var Q13;
            Q13=makeQuery(id+"F1.opExtrude","SWEPT_EDGE",EDGE,{"disambiguationData":[OSD([sQuery(id+"F0.wireOp",EDGE,"E0.bottom"),sQuery(id+"F0.wireOp",EDGE,"E0.left")])]});
            var Q14;
            Q14=makeQuery(id+"F7.boolean.opBoolean","COPY",EDGE,{"derivedFrom":makeQuery(id+"F7.opExtrude","SWEPT_EDGE",EDGE,{"disambiguationData":[OSD([sQuery(id+"F0.wireOp",EDGE,"E0.top"),sQuery(id+"F6.wireOp",EDGE,"E7.top"),sQuery(id+"F6.wireOp",EDGE,"E7.right")])]})});
            var Q15;
            Q15=makeQuery(id+"F7.boolean.opBoolean","COPY",EDGE,{"derivedFrom":makeQuery(id+"F7.opExtrude","CAP_EDGE",EDGE,{"disambiguationData":[OSD([sQuery(id+"F6.wireOp",EDGE,"E7.top")])],"isStart":false})});
            var Q16;
            Q16=makeQuery(id+"F7.boolean.opBoolean","COPY",EDGE,{"derivedFrom":makeQuery(id+"F7.opExtrude","CAP_EDGE",EDGE,{"disambiguationData":[OSD([sQuery(id+"F6.wireOp",EDGE,"E7.bottom")])],"isStart":false})});
            var Q17;
            Q17=makeQuery(id+"F7.boolean.opBoolean","COPY",EDGE,{"derivedFrom":makeQuery(id+"F7.opExtrude","SWEPT_EDGE",EDGE,{"disambiguationData":[OSD([sQuery(id+"F0.wireOp",EDGE,"E0.bottom"),sQuery(id+"F6.wireOp",EDGE,"E7.bottom"),sQuery(id+"F6.wireOp",EDGE,"E7.right")])]})});
            chamfer(context, id + "F14", {"entities" : qUnion([Q0, Q1, Q2, Q3, Q4, Q5, Q6, Q7, Q8, Q9, Q10, Q11, Q12, Q13, Q14, Q15, Q16, Q17]), "width" : 0.5 * mm, "tangentPropagation" : true});
        }
    });
